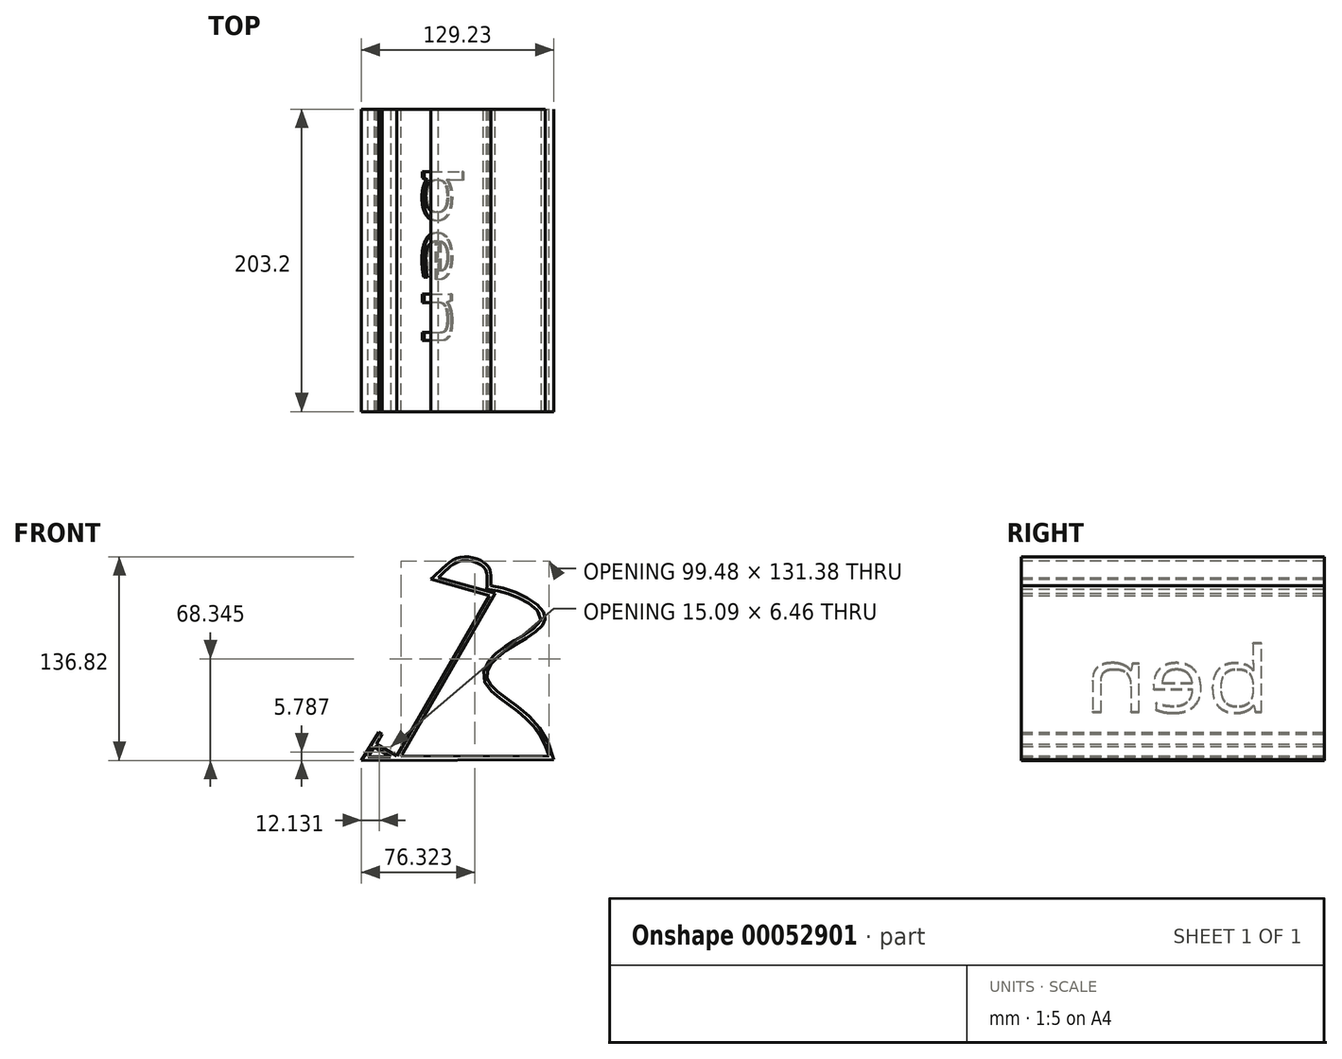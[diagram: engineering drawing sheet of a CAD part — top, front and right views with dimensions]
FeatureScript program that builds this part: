
annotation { "Feature Type Name" : "Feature", "Feature Type Description" : "" }
export const myFeature = defineFeature(function(context is Context, id is Id, definition is map)
    precondition{}
    {
        {
            var Q0;
            Q0=qCreatedBy(makeId("Front.planeOp"),FACE);
            var sketch = newSketch(context, id + "F0", { "sketchPlane" : qUnion([Q0])});
            skLineSegment(sketch, "E0.bottom", {"start": v(-48.07, 27.2) * mm, "end": v(28.13, 27.2) * mm, "construction": true});
            skLineSegment(sketch, "E0.top", {"start": v(-48.07, -60.38) * mm, "end": v(28.13, -60.38) * mm, "construction": true});
            skLineSegment(sketch, "E0.right", {"start": v(28.13, 27.2) * mm, "end": v(28.13, -60.38) * mm, "construction": true});
            skLineSegment(sketch, "E1", {"start": v(28.68, 49.29) * mm, "end": v(-33.55, -58.5) * mm});
            skLineSegment(sketch, "E2", {"start": v(-47.3, -50.56) * mm, "end": v(-43.49, -43.96) * mm});
            skLineSegment(sketch, "E3", {"start": v(-43.49, -43.96) * mm, "end": v(-45.69, -42.7) * mm});
            skLineSegment(sketch, "E4", {"start": v(-47.3, -50.56) * mm, "end": v(-33.55, -58.5) * mm});
            skLineSegment(sketch, "E5", {"start": v(-48.07, 27.2) * mm, "end": v(-48.07, -60.38) * mm, "construction": true});
            skPoint(sketch, "E6.1.internal.snap0", {"position": v(-9.97, -60.38) * mm});
            skLineSegment(sketch, "E7", {"start": v(-10.78, 60.11) * mm, "end": v(28.68, 49.29) * mm});
            skFitSpline(sketch, "E8", {"points": [v(-10.78, 60.11) * mm, v(7.85, 74.56) * mm, v(27.12, 69.41) * mm, v(29.44, 55.74) * mm], "startDerivative": vector(44.98, 35.08) * mm, "endDerivative": vector(-3.72, -58.28) * mm});
            skFitSpline(sketch, "E9", {"points": [v(29.44, 55.74) * mm, v(66.07, 34.13) * mm, v(37.42, 10.56) * mm, v(28.13, -9.1) * mm, v(71.77, -61.05) * mm], "startDerivative": vector(187.4, -19) * mm, "endDerivative": vector(57.6, -298.34) * mm});
            skLineSegment(sketch, "E10", {"start": v(-45.69, -42.7) * mm, "end": v(-57.46, -61.61) * mm});
            skLineSegment(sketch, "E11", {"start": v(-57.46, -61.61) * mm, "end": v(71.77, -61.05) * mm});
            skSolve(sketch);
        }
        {
            var Q0;
            Q0 = qSketchRegion(id + "F0", true);
            extrude(context, id + "F1", {"entities" : qUnion([Q0]), "depth" : 203.2 * mm});
        }
        {
            var Q0;
            Q0=makeQuery(id+"F1.opExtrude","CAP_FACE",FACE,{"disambiguationData":[OSD([sQuery(id+"F0.wireOp",EDGE,"E1"),sQuery(id+"F0.wireOp",EDGE,"E2"),sQuery(id+"F0.wireOp",EDGE,"E3"),sQuery(id+"F0.wireOp",EDGE,"E4"),sQuery(id+"F0.wireOp",EDGE,"E7"),sQuery(id+"F0.wireOp",EDGE,"E8"),sQuery(id+"F0.wireOp",EDGE,"E9"),sQuery(id+"F0.wireOp",EDGE,"E10"),sQuery(id+"F0.wireOp",EDGE,"E11")])],"isStart":false});
            var Q1;
            Q1=makeQuery(id+"F1.opExtrude","CAP_FACE",FACE,{"disambiguationData":[OSD([sQuery(id+"F0.wireOp",EDGE,"E1"),sQuery(id+"F0.wireOp",EDGE,"E2"),sQuery(id+"F0.wireOp",EDGE,"E3"),sQuery(id+"F0.wireOp",EDGE,"E4"),sQuery(id+"F0.wireOp",EDGE,"E7"),sQuery(id+"F0.wireOp",EDGE,"E8"),sQuery(id+"F0.wireOp",EDGE,"E9"),sQuery(id+"F0.wireOp",EDGE,"E10"),sQuery(id+"F0.wireOp",EDGE,"E11")])],"isStart":true});
            shell(context, id + "F2", {"entities" : qUnion([Q0, Q1]), "thickness" : 2.54 * mm});
        }
        {
            var Q0;
            Q0=makeQuery(id+"F1.opExtrude","SWEPT_FACE",FACE,{"disambiguationData":[OSD([sQuery(id+"F0.wireOp",EDGE,"E1")])]});
            var sketch = newSketch(context, id + "F3", { "sketchPlane" : qUnion([Q0])});
            skText(sketch, "E12", { "text": "ben", "fontName": "OpenSans-Regular.ttf"});
            const initialGuessF3  = {"E12": [0.03597, -0.03314, 1, 0, 0.0504]};
            skSetInitialGuess(sketch, initialGuessF3);
            skSolve(sketch);
        }
        {
            var Q0;
            Q0 = qSketchRegion(id + "F3", true);
            extrude(context, id + "F4", {"entities" : qUnion([Q0]), "operationType" : NewBodyOperationType.REMOVE, "oppositeDirection" : true, "depth" : 1.27 * mm});
        }
    });
